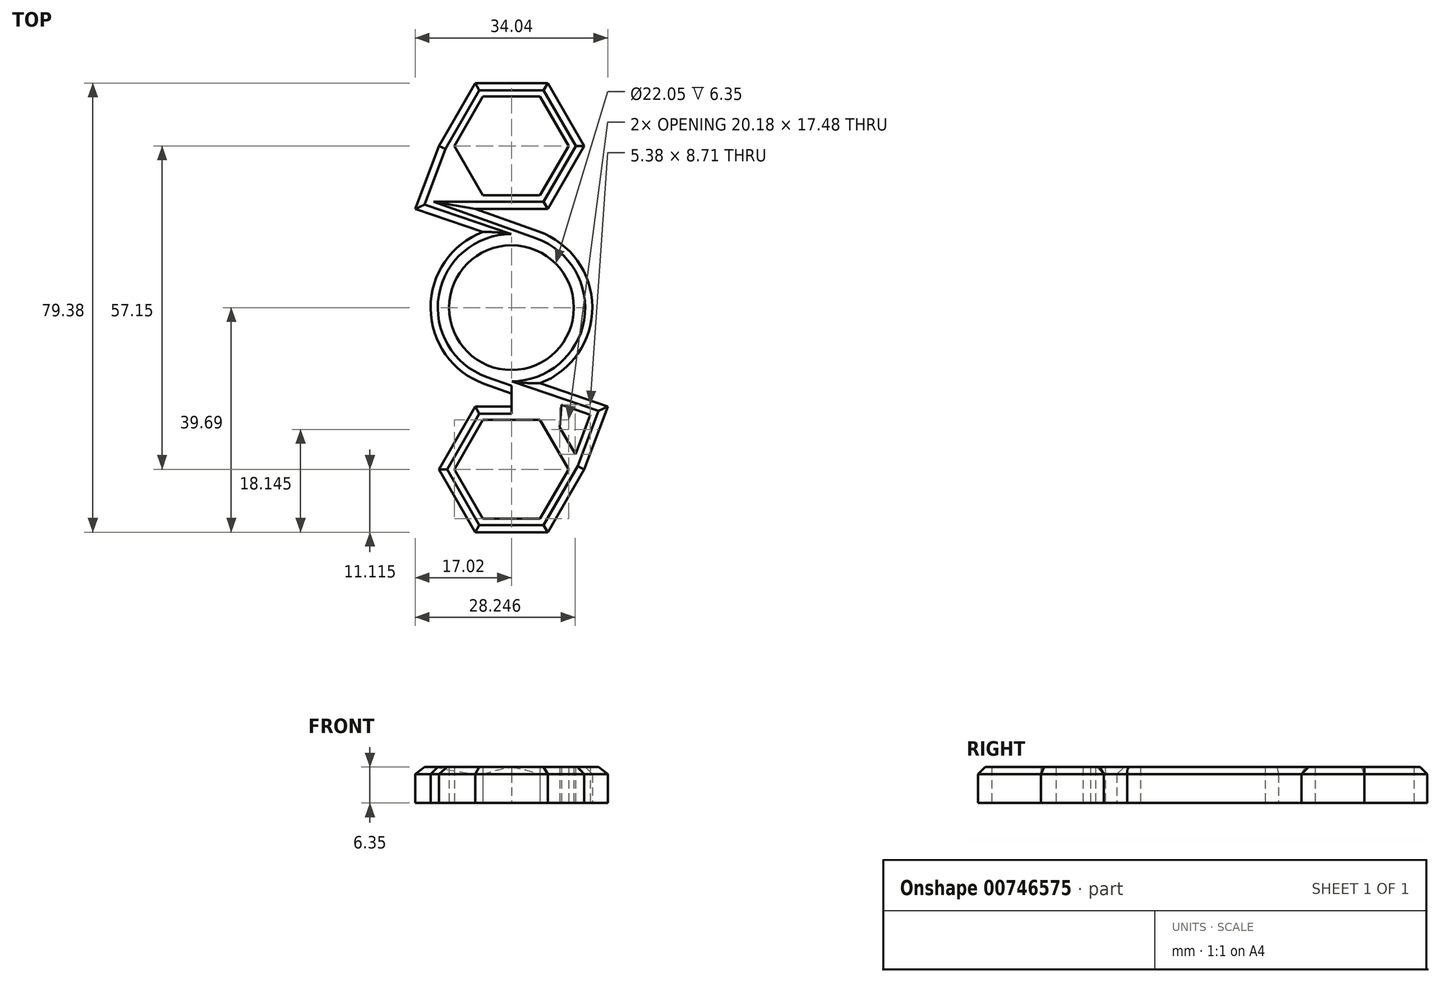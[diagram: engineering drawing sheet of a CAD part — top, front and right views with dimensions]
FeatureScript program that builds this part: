
annotation { "Feature Type Name" : "Feature", "Feature Type Description" : "" }
export const myFeature = defineFeature(function(context is Context, id is Id, definition is map)
    precondition{}
    {
        {
            var Q0;
            Q0=qCreatedBy(makeId("Top.planeOp"),FACE);
            var sketch = newSketch(context, id + "F0", { "sketchPlane" : qUnion([Q0])});
            skCircle(sketch, "E0", {"center": v(0, 0) * mm, "radius": 11.02 * mm});
            skCircle(sketch, "E1", {"center": v(0, 0) * mm, "radius": 14.29 * mm});
            skCircle(sketch, "E2.cCircle", {"center": v(0, 28.58) * mm, "radius": 8.74 * mm, "construction": true});
            skLineSegment(sketch, "E2.0", {"start": v(5.04, 19.84) * mm, "end": v(-5.04, 19.84) * mm});
            skLineSegment(sketch, "E2.1", {"start": v(-5.04, 19.84) * mm, "end": v(-10.09, 28.58) * mm});
            skLineSegment(sketch, "E2.2", {"start": v(-10.09, 28.58) * mm, "end": v(-5.04, 37.31) * mm});
            skLineSegment(sketch, "E2.3", {"start": v(-5.04, 37.31) * mm, "end": v(5.04, 37.31) * mm});
            skLineSegment(sketch, "E2.4", {"start": v(5.04, 37.31) * mm, "end": v(10.09, 28.58) * mm});
            skLineSegment(sketch, "E2.5", {"start": v(10.09, 28.58) * mm, "end": v(5.04, 19.84) * mm});
            skPoint(sketch, "E2.0.midPoint", {"position": v(0, 19.84) * mm});
            skCircle(sketch, "E3.cCircle", {"center": v(0, 28.58) * mm, "radius": 11.11 * mm, "construction": true});
            skLineSegment(sketch, "E3.0", {"start": v(6.42, 17.46) * mm, "end": v(-6.42, 17.46) * mm});
            skLineSegment(sketch, "E3.1", {"start": v(-6.42, 17.46) * mm, "end": v(-12.83, 28.57) * mm});
            skLineSegment(sketch, "E3.2", {"start": v(-12.83, 28.57) * mm, "end": v(-6.42, 39.69) * mm});
            skLineSegment(sketch, "E3.3", {"start": v(-6.42, 39.69) * mm, "end": v(6.42, 39.69) * mm});
            skLineSegment(sketch, "E3.4", {"start": v(6.42, 39.69) * mm, "end": v(12.83, 28.58) * mm});
            skLineSegment(sketch, "E3.5", {"start": v(12.83, 28.57) * mm, "end": v(6.42, 17.46) * mm});
            skPoint(sketch, "E3.0.midPoint", {"position": v(0, 17.46) * mm});
            skPoint(sketch, "E4.1.0", {"position": v(0, -17.46) * mm});
            skCircle(sketch, "E4.1.1", {"center": v(0, -28.58) * mm, "radius": 8.74 * mm, "construction": true});
            skLineSegment(sketch, "E4.1.2", {"start": v(-12.83, -28.57) * mm, "end": v(-6.42, -17.46) * mm});
            skLineSegment(sketch, "E4.1.3", {"start": v(6.42, -39.69) * mm, "end": v(-6.42, -39.69) * mm});
            skLineSegment(sketch, "E4.1.4", {"start": v(5.04, -19.84) * mm, "end": v(10.09, -28.58) * mm});
            skLineSegment(sketch, "E4.1.5", {"start": v(-10.09, -28.58) * mm, "end": v(-5.04, -19.84) * mm});
            skCircle(sketch, "E4.1.6", {"center": v(0, -28.58) * mm, "radius": 11.11 * mm, "construction": true});
            skLineSegment(sketch, "E4.1.7", {"start": v(6.42, -17.46) * mm, "end": v(12.83, -28.57) * mm});
            skPoint(sketch, "E4.1.8", {"position": v(0, -19.84) * mm});
            skLineSegment(sketch, "E4.1.9", {"start": v(-5.04, -19.84) * mm, "end": v(5.04, -19.84) * mm});
            skLineSegment(sketch, "E4.1.10", {"start": v(10.09, -28.58) * mm, "end": v(5.04, -37.31) * mm});
            skLineSegment(sketch, "E4.1.11", {"start": v(-6.42, -39.69) * mm, "end": v(-12.83, -28.58) * mm});
            skLineSegment(sketch, "E4.1.12", {"start": v(5.04, -37.31) * mm, "end": v(-5.04, -37.31) * mm});
            skLineSegment(sketch, "E4.1.13", {"start": v(-5.04, -37.31) * mm, "end": v(-10.09, -28.58) * mm});
            skLineSegment(sketch, "E4.1.14", {"start": v(-6.42, -17.46) * mm, "end": v(6.42, -17.46) * mm});
            skLineSegment(sketch, "E4.1.15", {"start": v(12.83, -28.57) * mm, "end": v(6.42, -39.69) * mm});
            skSolve(sketch);
        }
        {
            var Q0;
            Q0=makeQuery(id+"F0.imprint","IMPRINT",FACE,{"disambiguationData":[TD([[makeQuery(id+"F0.imprint","IMPRINT",EDGE,{"derivedFrom":sQuery(id+"F0.wireOp",EDGE,"E0")}),1.0]])]});
            var sketch = newSketch(context, id + "F1", { "sketchPlane" : qUnion([Q0])});
            skLineSegment(sketch, "E5.0", {"start": v(6.42, 39.69) * mm, "end": v(12.83, 28.58) * mm});
            skLineSegment(sketch, "E5.1", {"start": v(12.83, 28.57) * mm, "end": v(6.42, 17.46) * mm});
            skCircle(sketch, "E5.2", {"center": v(0, 0) * mm, "radius": 11.02 * mm});
            skCircle(sketch, "E5.3", {"center": v(0, 0) * mm, "radius": 14.29 * mm});
            skCircle(sketch, "E5.4", {"center": v(0, 28.58) * mm, "radius": 8.74 * mm});
            skLineSegment(sketch, "E5.5", {"start": v(5.04, 19.84) * mm, "end": v(-5.04, 19.84) * mm});
            skLineSegment(sketch, "E5.6", {"start": v(-6.42, 39.69) * mm, "end": v(6.42, 39.69) * mm});
            skLineSegment(sketch, "E5.7", {"start": v(-12.83, -28.57) * mm, "end": v(-6.42, -17.46) * mm});
            skLineSegment(sketch, "E5.8", {"start": v(5.04, -19.84) * mm, "end": v(10.09, -28.58) * mm});
            skCircle(sketch, "E5.9", {"center": v(0, -28.58) * mm, "radius": 11.11 * mm});
            skLineSegment(sketch, "E5.10", {"start": v(10.09, -28.58) * mm, "end": v(5.04, -37.31) * mm});
            skLineSegment(sketch, "E5.11", {"start": v(5.04, -37.31) * mm, "end": v(-5.04, -37.31) * mm});
            skLineSegment(sketch, "E5.12", {"start": v(-6.42, -17.46) * mm, "end": v(6.42, -17.46) * mm});
            skLineSegment(sketch, "E5.13", {"start": v(-5.04, 19.84) * mm, "end": v(-10.09, 28.58) * mm});
            skLineSegment(sketch, "E5.14", {"start": v(-10.09, 28.58) * mm, "end": v(-5.04, 37.31) * mm});
            skLineSegment(sketch, "E5.15", {"start": v(-5.04, 37.31) * mm, "end": v(5.04, 37.31) * mm});
            skLineSegment(sketch, "E5.16", {"start": v(5.04, 37.31) * mm, "end": v(10.09, 28.58) * mm});
            skLineSegment(sketch, "E5.17", {"start": v(10.09, 28.58) * mm, "end": v(5.04, 19.84) * mm});
            skCircle(sketch, "E5.18", {"center": v(0, 28.58) * mm, "radius": 11.11 * mm});
            skLineSegment(sketch, "E5.19", {"start": v(6.42, 17.46) * mm, "end": v(-6.42, 17.46) * mm});
            skLineSegment(sketch, "E5.20", {"start": v(-6.42, 17.46) * mm, "end": v(-12.83, 28.57) * mm});
            skLineSegment(sketch, "E5.21", {"start": v(-12.83, 28.57) * mm, "end": v(-6.42, 39.69) * mm});
            skLineSegment(sketch, "E5.22", {"start": v(-5.04, -37.31) * mm, "end": v(-10.09, -28.58) * mm});
            skLineSegment(sketch, "E5.23", {"start": v(-6.42, -39.69) * mm, "end": v(-12.83, -28.58) * mm});
            skLineSegment(sketch, "E5.24", {"start": v(-5.04, -19.84) * mm, "end": v(5.04, -19.84) * mm});
            skLineSegment(sketch, "E5.25", {"start": v(6.42, -17.46) * mm, "end": v(12.83, -28.57) * mm});
            skLineSegment(sketch, "E5.26", {"start": v(-10.09, -28.58) * mm, "end": v(-5.04, -19.84) * mm});
            skLineSegment(sketch, "E5.27", {"start": v(12.83, -28.57) * mm, "end": v(6.42, -39.69) * mm});
            skLineSegment(sketch, "E5.28", {"start": v(6.42, -39.69) * mm, "end": v(-6.42, -39.69) * mm});
            skCircle(sketch, "E5.29", {"center": v(0, -28.58) * mm, "radius": 8.74 * mm});
            skLineSegment(sketch, "E6", {"start": v(6.42, -17.46) * mm, "end": v(-5.04, -13.37) * mm});
            skLineSegment(sketch, "E7", {"start": v(-5.04, -13.37) * mm, "end": v(5.04, -13.37) * mm});
            skLineSegment(sketch, "E8", {"start": v(5.04, -13.37) * mm, "end": v(17.02, -17.46) * mm});
            skLineSegment(sketch, "E9", {"start": v(17.02, -17.46) * mm, "end": v(12.83, -28.57) * mm});
            skLineSegment(sketch, "E10.1.0", {"start": v(5.04, 13.37) * mm, "end": v(-5.04, 13.37) * mm});
            skLineSegment(sketch, "E10.1.1", {"start": v(-6.42, 17.46) * mm, "end": v(5.04, 13.37) * mm});
            skLineSegment(sketch, "E10.1.2", {"start": v(-5.04, 13.37) * mm, "end": v(-17.02, 17.46) * mm});
            skLineSegment(sketch, "E10.1.3", {"start": v(-17.02, 17.46) * mm, "end": v(-12.83, 28.57) * mm});
            skLineSegment(sketch, "E11", {"start": v(11.29, -25.9) * mm, "end": v(13.92, -18.93) * mm});
            skLineSegment(sketch, "E12", {"start": v(13.92, -18.93) * mm, "end": v(8.83, -17.19) * mm});
            skLineSegment(sketch, "E13", {"start": v(8.83, -17.19) * mm, "end": v(8.53, -21.13) * mm});
            skLineSegment(sketch, "E14", {"start": v(0, -15.17) * mm, "end": v(0, -17.46) * mm});
            skSolve(sketch);
        }
        {
            var Q0;
            Q0=makeQuery(id+"F0.imprint","IMPRINT",FACE,{"disambiguationData":[TD([[makeQuery(id+"F0.imprint","IMPRINT",EDGE,{"derivedFrom":sQuery(id+"F0.wireOp",EDGE,"E2.0")}),1.0]])]});
            extrude(context, id + "F2", {"entities" : qUnion([Q0]), "depth" : 6.35 * mm, "offsetDistance" : 25.4 * mm});
        }
        {
            var Q0;
            {var subQ7=sQuery(id+"F1.wireOp",EDGE,"E10.1.2");Q0=makeQuery(id+"F1.imprint","IMPRINT",FACE,{"disambiguationData":[TD([[makeQuery(id+"F1.imprint","IMPRINT",EDGE,{"derivedFrom":subQ7}),-1.0]])]});}
            var Q1;
            {var subQ0=sQuery(id+"F1.wireOp",EDGE,"E5.3");var subQ1=makeQuery(id+"F1.imprint","INTERSECT",VERTEX,{"derivedFrom":[subQ0,sQuery(id+"F1.wireOp",EDGE,"E10.1.1")]});Q1=makeQuery(id+"F1.imprint","IMPRINT",FACE,{"disambiguationData":[TD([[makeQuery(id+"F1.imprint","IMPRINT",EDGE,{"disambiguationData":[TD([[subQ1,1.0]])],"derivedFrom":subQ0}),1.0]])]});}
            var Q2;
            Q2=makeQuery(id+"F1.imprint","IMPRINT",FACE,{"disambiguationData":[TD([[makeQuery(id+"F1.imprint","IMPRINT",EDGE,{"derivedFrom":sQuery(id+"F1.wireOp",EDGE,"E5.2")}),-1.0]])]});
            var Q3;
            {var subQ0=sQuery(id+"F1.wireOp",EDGE,"E7");var subQ1=sQuery(id+"F1.wireOp",EDGE,"E5.3");var subQ2=makeQuery(id+"F1.imprint","INTERSECT",VERTEX,{"derivedFrom":[subQ1,subQ0]});Q3=makeQuery(id+"F1.imprint","IMPRINT",FACE,{"disambiguationData":[TD([[makeQuery(id+"F1.imprint","IMPRINT",EDGE,{"disambiguationData":[TD([[subQ2,-1.0]])],"derivedFrom":subQ1}),1.0]])]});}
            var Q4;
            {var subQ7=sQuery(id+"F1.wireOp",EDGE,"E8");Q4=makeQuery(id+"F1.imprint","IMPRINT",FACE,{"disambiguationData":[TD([[makeQuery(id+"F1.imprint","IMPRINT",EDGE,{"derivedFrom":subQ7}),-1.0]])]});}
            var Q5;
            {var subQ0=sQuery(id+"F1.wireOp",EDGE,"E5.28");var subQ1=sQuery(id+"F1.wireOp",EDGE,"E5.9");var subQ2=makeQuery(id+"F1.imprint","INTERSECT",VERTEX,{"derivedFrom":[subQ1,subQ0]});Q5=makeQuery(id+"F1.imprint","IMPRINT",FACE,{"disambiguationData":[TD([[makeQuery(id+"F1.imprint","IMPRINT",EDGE,{"disambiguationData":[TD([[subQ2,-1.0]])],"derivedFrom":subQ1}),-1.0]])]});}
            var Q6;
            {var subQ5=sQuery(id+"F1.wireOp",EDGE,"E5.8");var subQ13=sQuery(id+"F1.wireOp",EDGE,"E5.24");var subQ14=makeQuery(id+"F1.imprint","INTERSECT",VERTEX,{"derivedFrom":[subQ5,subQ13]});Q6=makeQuery(id+"F1.imprint","IMPRINT",FACE,{"disambiguationData":[TD([[makeQuery(id+"F1.imprint","IMPRINT",EDGE,{"disambiguationData":[TD([[subQ14,-1.0]])],"derivedFrom":subQ5}),1.0]])]});}
            var Q7;
            {var subQ0=sQuery(id+"F1.wireOp",EDGE,"E5.27");var subQ1=sQuery(id+"F1.wireOp",EDGE,"E5.9");var subQ2=makeQuery(id+"F1.imprint","INTERSECT",VERTEX,{"derivedFrom":[subQ1,subQ0]});Q7=makeQuery(id+"F1.imprint","IMPRINT",FACE,{"disambiguationData":[TD([[makeQuery(id+"F1.imprint","IMPRINT",EDGE,{"disambiguationData":[TD([[subQ2,-1.0]])],"derivedFrom":subQ1}),-1.0]])]});}
            var Q8;
            {var subQ0=sQuery(id+"F1.wireOp",EDGE,"E5.28");var subQ1=sQuery(id+"F1.wireOp",EDGE,"E5.9");var subQ2=makeQuery(id+"F1.imprint","INTERSECT",VERTEX,{"derivedFrom":[subQ1,subQ0]});Q8=makeQuery(id+"F1.imprint","IMPRINT",FACE,{"disambiguationData":[TD([[makeQuery(id+"F1.imprint","IMPRINT",EDGE,{"disambiguationData":[TD([[subQ2,1.0]])],"derivedFrom":subQ1}),-1.0]])]});}
            var Q9;
            {var subQ0=sQuery(id+"F1.wireOp",EDGE,"E5.23");var subQ1=sQuery(id+"F1.wireOp",EDGE,"E5.7");var subQ2=makeQuery(id+"F1.imprint","INTERSECT",VERTEX,{"derivedFrom":[subQ1,subQ0]});Q9=makeQuery(id+"F1.imprint","IMPRINT",FACE,{"disambiguationData":[TD([[makeQuery(id+"F1.imprint","IMPRINT",EDGE,{"disambiguationData":[TD([[subQ2,-1.0]])],"derivedFrom":subQ1}),-1.0]])]});}
            var Q10;
            {var subQ0=sQuery(id+"F1.wireOp",EDGE,"E5.12");var subQ1=sQuery(id+"F1.wireOp",EDGE,"E5.7");var subQ2=makeQuery(id+"F1.imprint","INTERSECT",VERTEX,{"derivedFrom":[subQ1,subQ0]});Q10=makeQuery(id+"F1.imprint","IMPRINT",FACE,{"disambiguationData":[TD([[makeQuery(id+"F1.imprint","IMPRINT",EDGE,{"disambiguationData":[TD([[subQ2,1.0]])],"derivedFrom":subQ1}),-1.0]])]});}
            var Q11;
            {var subQ0=sQuery(id+"F1.wireOp",EDGE,"E5.12");var subQ1=sQuery(id+"F1.wireOp",EDGE,"E5.9");var subQ2=makeQuery(id+"F1.imprint","INTERSECT",VERTEX,{"derivedFrom":[subQ1,subQ0]});Q11=makeQuery(id+"F1.imprint","IMPRINT",FACE,{"disambiguationData":[TD([[makeQuery(id+"F1.imprint","IMPRINT",EDGE,{"disambiguationData":[TD([[subQ2,1.0]])],"derivedFrom":subQ1}),-1.0]])]});}
            var Q12;
            {var subQ3=sQuery(id+"F1.wireOp",EDGE,"E14");Q12=makeQuery(id+"F1.imprint","IMPRINT",FACE,{"disambiguationData":[TD([[makeQuery(id+"F1.imprint","IMPRINT",EDGE,{"derivedFrom":subQ3}),1.0]])]});}
            extrude(context, id + "F3", {"entities" : qUnion([Q0, Q1, Q2, Q3, Q4, Q5, Q6, Q7, Q8, Q9, Q10, Q11, Q12]), "operationType" : NewBodyOperationType.ADD, "depth" : 6.35 * mm, "offsetDistance" : 25.4 * mm});
        }
        {
            var Q0;
            Q0=makeQuery(id+"F3.opExtrude","CAP_EDGE",EDGE,{"disambiguationData":[OSD([sQuery(id+"F1.wireOp",EDGE,"E10.1.2")])],"isStart":false});
            var Q1;
            Q1=makeQuery(id+"F3.opExtrude","CAP_EDGE",EDGE,{"disambiguationData":[OSD([sQuery(id+"F1.wireOp",EDGE,"E10.1.3")])],"isStart":false});
            var Q2;
            Q2=makeQuery(id+"F2.opExtrude","CAP_EDGE",EDGE,{"disambiguationData":[OSD([sQuery(id+"F0.wireOp",EDGE,"E3.2")])],"isStart":false});
            var Q3;
            Q3=makeQuery(id+"F2.opExtrude","CAP_EDGE",EDGE,{"disambiguationData":[OSD([sQuery(id+"F0.wireOp",EDGE,"E3.3")])],"isStart":false});
            var Q4;
            Q4=makeQuery(id+"F2.opExtrude","CAP_EDGE",EDGE,{"disambiguationData":[OSD([sQuery(id+"F0.wireOp",EDGE,"E3.4")])],"isStart":false});
            var Q5;
            Q5=makeQuery(id+"F2.opExtrude","CAP_EDGE",EDGE,{"disambiguationData":[OSD([sQuery(id+"F0.wireOp",EDGE,"E3.5")])],"isStart":false});
            var Q6;
            Q6=makeQuery(id+"F2.opExtrude","CAP_EDGE",EDGE,{"disambiguationData":[OSD([sQuery(id+"F0.wireOp",EDGE,"E3.0")])],"isStart":false});
            var Q7;
            Q7=makeQuery(id+"F3.opExtrude","CAP_EDGE",EDGE,{"disambiguationData":[OSD([sQuery(id+"F1.wireOp",EDGE,"E10.1.1")])],"isStart":false});
            var Q8;
            {var subQ0=sQuery(id+"F1.wireOp",EDGE,"E5.3");var subQ1=makeQuery(id+"F1.imprint","INTERSECT",VERTEX,{"derivedFrom":[subQ0,sQuery(id+"F1.wireOp",EDGE,"E10.1.0")]});Q8=makeQuery(id+"F3.opExtrude","CAP_EDGE",EDGE,{"disambiguationData":[OSD([subQ0]),TDD([makeQuery(id+"F1.imprint","IMPRINT",EDGE,{"disambiguationData":[TD([[makeQuery(id+"F1.imprint","INTERSECT",VERTEX,{"derivedFrom":[subQ0,sQuery(id+"F1.wireOp",EDGE,"E10.1.1")]}),1.0]])],"derivedFrom":subQ0}),makeQuery(id+"F1.imprint","IMPRINT",EDGE,{"disambiguationData":[TD([[subQ1,1.0]])],"derivedFrom":subQ0})])],"isStart":false});}
            var Q9;
            {var subQ0=sQuery(id+"F1.wireOp",EDGE,"E5.3");var subQ1=makeQuery(id+"F1.imprint","INTERSECT",VERTEX,{"derivedFrom":[subQ0,sQuery(id+"F1.wireOp",EDGE,"E7")]});Q9=makeQuery(id+"F3.opExtrude","CAP_EDGE",EDGE,{"disambiguationData":[OSD([subQ0]),TDD([makeQuery(id+"F1.imprint","IMPRINT",EDGE,{"disambiguationData":[TD([[subQ1,1.0]])],"derivedFrom":subQ0}),makeQuery(id+"F1.imprint","IMPRINT",EDGE,{"disambiguationData":[TD([[subQ1,-1.0]])],"derivedFrom":subQ0})])],"isStart":false});}
            var Q10;
            Q10=makeQuery(id+"F3.opExtrude","CAP_EDGE",EDGE,{"disambiguationData":[OSD([sQuery(id+"F1.wireOp",EDGE,"E5.27")])],"isStart":false});
            var Q11;
            Q11=makeQuery(id+"F3.opExtrude","CAP_EDGE",EDGE,{"disambiguationData":[OSD([sQuery(id+"F1.wireOp",EDGE,"E5.28")])],"isStart":false});
            var Q12;
            Q12=makeQuery(id+"F3.opExtrude","CAP_EDGE",EDGE,{"disambiguationData":[OSD([sQuery(id+"F1.wireOp",EDGE,"E5.23")])],"isStart":false});
            var Q13;
            Q13=makeQuery(id+"F3.opExtrude","CAP_EDGE",EDGE,{"disambiguationData":[OSD([sQuery(id+"F1.wireOp",EDGE,"E5.7")])],"isStart":false});
            var Q14;
            Q14=makeQuery(id+"F3.opExtrude","CAP_EDGE",EDGE,{"disambiguationData":[OSD([sQuery(id+"F1.wireOp",EDGE,"E5.12")])],"isStart":false});
            var Q15;
            Q15=makeQuery(id+"F3.opExtrude","CAP_EDGE",EDGE,{"disambiguationData":[OSD([sQuery(id+"F1.wireOp",EDGE,"E9")])],"isStart":false});
            var Q16;
            Q16=makeQuery(id+"F3.opExtrude","CAP_EDGE",EDGE,{"disambiguationData":[OSD([sQuery(id+"F1.wireOp",EDGE,"E8")])],"isStart":false});
            var Q17;
            Q17=makeQuery(id+"F3.opExtrude","CAP_EDGE",EDGE,{"disambiguationData":[OSD([sQuery(id+"F1.wireOp",EDGE,"E6")])],"isStart":false});
            chamfer(context, id + "F4", {"entities" : qUnion([Q0, Q1, Q2, Q3, Q4, Q5, Q6, Q7, Q8, Q9, Q10, Q11, Q12, Q13, Q14, Q15, Q16, Q17]), "width" : 1.27 * mm, "tangentPropagation" : true});
        }
    });
